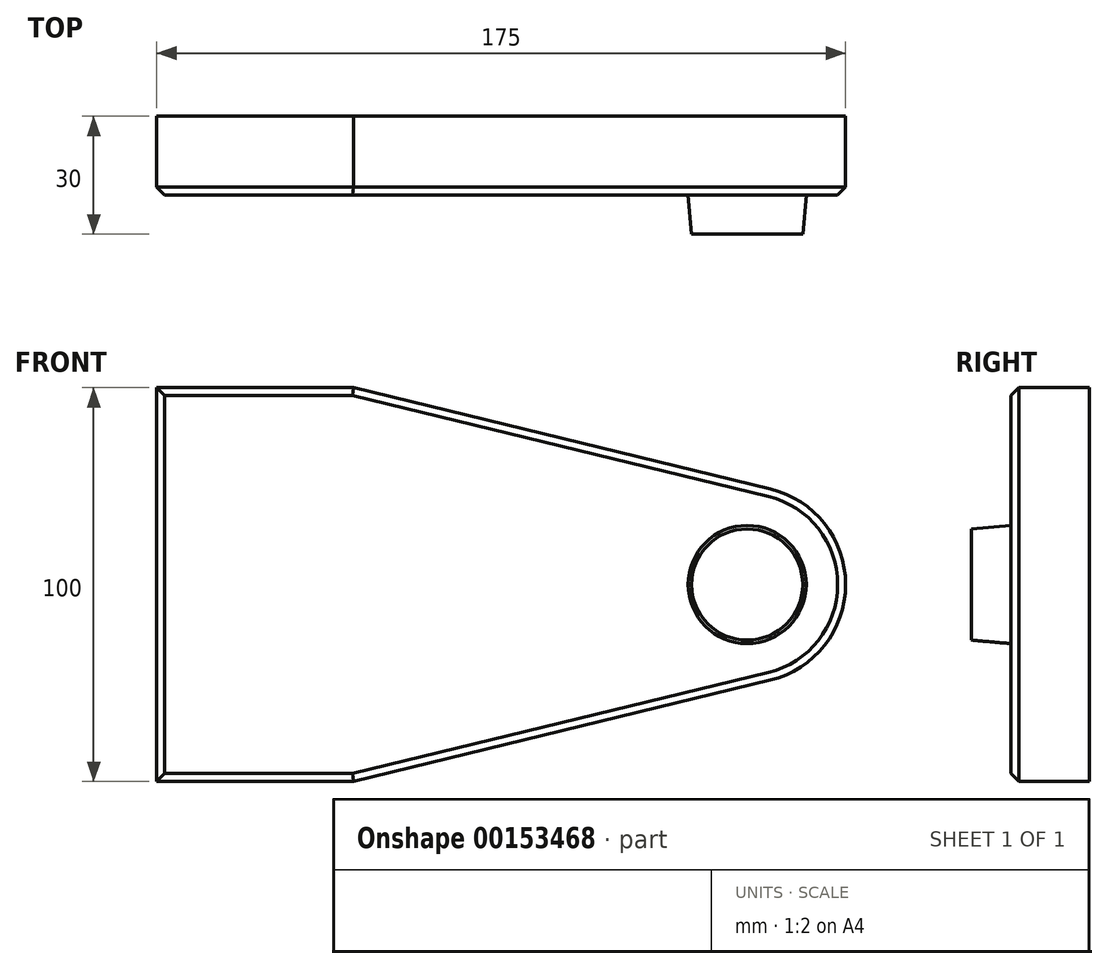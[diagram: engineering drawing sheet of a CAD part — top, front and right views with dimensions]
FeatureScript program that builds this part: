
annotation { "Feature Type Name" : "Feature", "Feature Type Description" : "" }
export const myFeature = defineFeature(function(context is Context, id is Id, definition is map)
    precondition{}
    {
        {
            var Q0;
            Q0=qCreatedBy(makeId("Front.planeOp"),FACE);
            var sketch = newSketch(context, id + "F0", { "sketchPlane" : qUnion([Q0])});
            skArc(sketch, "E0", {"start": v(105.9, -24.3) * mm, "mid": v(125, 0) * mm, "end": v(105.9, 24.3) * mm});
            skLineSegment(sketch, "E1", {"start": v(-50, -50) * mm, "end": v(-50, 50) * mm});
            skLineSegment(sketch, "E2", {"start": v(-50, 50) * mm, "end": v(0, 50) * mm});
            skLineSegment(sketch, "E3", {"start": v(0, 50) * mm, "end": v(105.9, 24.3) * mm});
            skLineSegment(sketch, "E4", {"start": v(-50, -50) * mm, "end": v(0, -50) * mm});
            skLineSegment(sketch, "E5", {"start": v(0, -50) * mm, "end": v(105.9, -24.3) * mm});
            skSolve(sketch);
        }
        {
            var Q0;
            Q0=makeQuery(id+"F0.imprint","IMPRINT",FACE,{"disambiguationData":[TD([[makeQuery(id+"F0.imprint","IMPRINT",EDGE,{"derivedFrom":sQuery(id+"F0.wireOp",EDGE,"E0")}),1.0]])]});
            extrude(context, id + "F1", {"entities" : qUnion([Q0]), "depth" : 20 * mm});
        }
        {
            var Q0;
            Q0=makeQuery(id+"F1.opExtrude","CAP_FACE",FACE,{"disambiguationData":[OSD([sQuery(id+"F0.wireOp",EDGE,"E0"),sQuery(id+"F0.wireOp",EDGE,"E1"),sQuery(id+"F0.wireOp",EDGE,"E2"),sQuery(id+"F0.wireOp",EDGE,"E3"),sQuery(id+"F0.wireOp",EDGE,"E4"),sQuery(id+"F0.wireOp",EDGE,"E5")])],"isStart":false});
            var sketch = newSketch(context, id + "F2", { "sketchPlane" : qUnion([Q0])});
            skCircle(sketch, "E6.converted", {"center": v(100, 0) * mm, "radius": 15 * mm});
            skSolve(sketch);
        }
        {
            var Q0;
            Q0 = qSketchRegion(id + "F2", true);
            extrude(context, id + "F3", {"entities" : qUnion([Q0]), "operationType" : NewBodyOperationType.ADD, "depth" : 10 * mm, "hasDraft" : true, "draftAngle" : 5 * degree, "draftPullDirection" : true});
        }
        {
            var Q0;
            Q0=makeQuery(id+"F1.opExtrude","CAP_EDGE",EDGE,{"disambiguationData":[OSD([sQuery(id+"F0.wireOp",EDGE,"E3")])],"isStart":false});
            var Q1;
            Q1=makeQuery(id+"F1.opExtrude","CAP_EDGE",EDGE,{"disambiguationData":[OSD([sQuery(id+"F0.wireOp",EDGE,"E2")])],"isStart":false});
            var Q2;
            Q2=makeQuery(id+"F1.opExtrude","CAP_EDGE",EDGE,{"disambiguationData":[OSD([sQuery(id+"F0.wireOp",EDGE,"E1")])],"isStart":false});
            var Q3;
            Q3=makeQuery(id+"F1.opExtrude","CAP_EDGE",EDGE,{"disambiguationData":[OSD([sQuery(id+"F0.wireOp",EDGE,"E4")])],"isStart":false});
            var Q4;
            Q4=makeQuery(id+"F1.opExtrude","CAP_EDGE",EDGE,{"disambiguationData":[OSD([sQuery(id+"F0.wireOp",EDGE,"E5")])],"isStart":false});
            var Q5;
            Q5=makeQuery(id+"F1.opExtrude","CAP_EDGE",EDGE,{"disambiguationData":[OSD([sQuery(id+"F0.wireOp",EDGE,"E0")])],"isStart":false});
            chamfer(context, id + "F4", {"entities" : qUnion([Q0, Q1, Q2, Q3, Q4, Q5]), "width" : 2 * mm, "tangentPropagation" : true});
        }
    });
